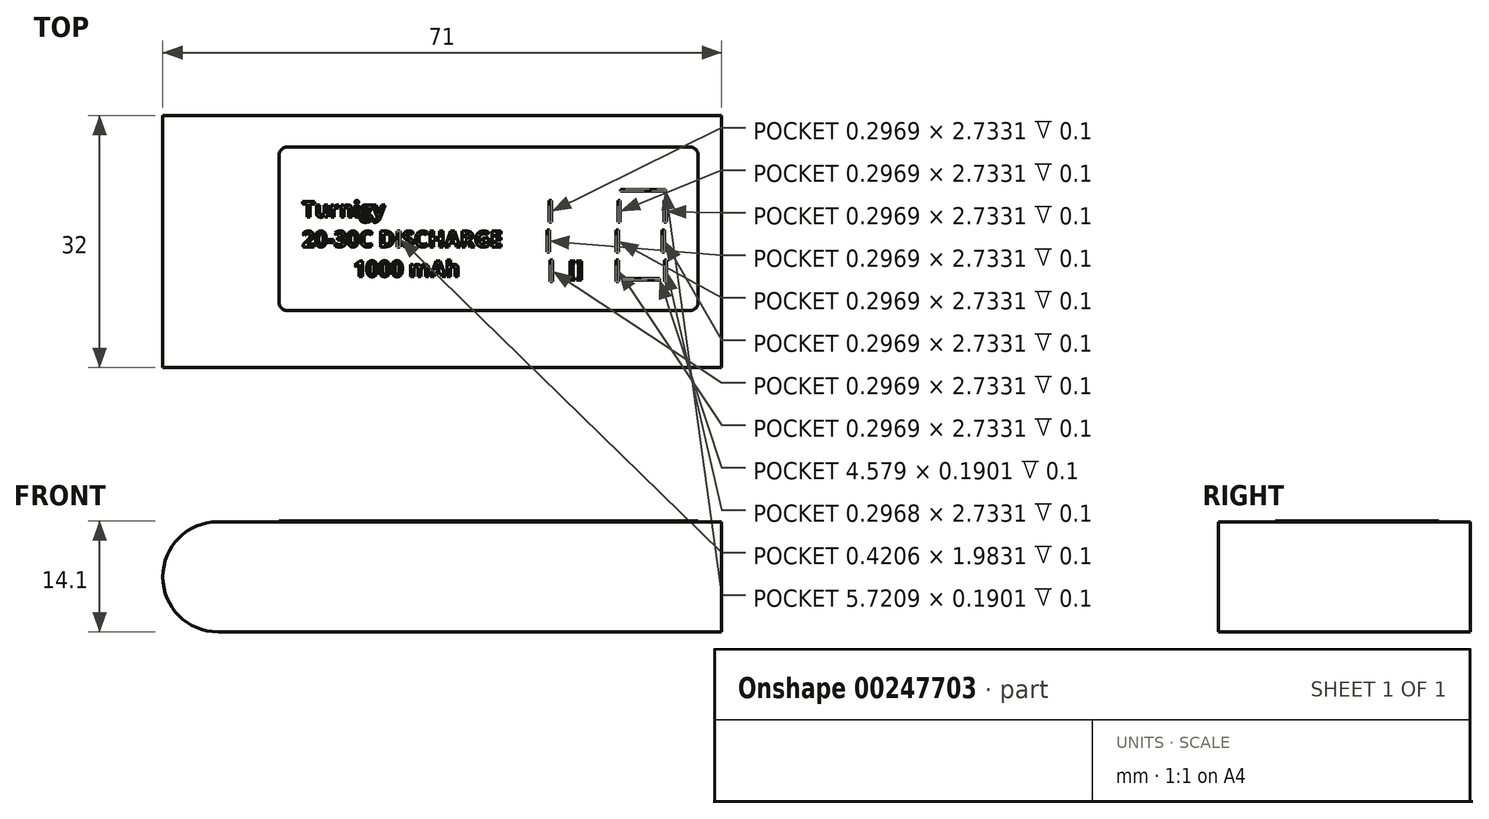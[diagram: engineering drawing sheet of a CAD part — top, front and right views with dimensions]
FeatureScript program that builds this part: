
annotation { "Feature Type Name" : "Feature", "Feature Type Description" : "" }
export const myFeature = defineFeature(function(context is Context, id is Id, definition is map)
    precondition{}
    {
        {
            var Q0;
            Q0=qCreatedBy(makeId("Top.planeOp"),FACE);
            var sketch = newSketch(context, id + "F0", { "sketchPlane" : qUnion([Q0])});
            skLineSegment(sketch, "E0.bottom", {"start": v(-40.56, 15.94) * mm, "end": v(30.44, 15.94) * mm});
            skLineSegment(sketch, "E0.top", {"start": v(-40.56, -16.06) * mm, "end": v(30.44, -16.06) * mm});
            skLineSegment(sketch, "E0.left", {"start": v(-40.56, 15.94) * mm, "end": v(-40.56, -16.06) * mm});
            skLineSegment(sketch, "E0.right", {"start": v(30.44, 15.94) * mm, "end": v(30.44, -16.06) * mm});
            skSolve(sketch);
        }
        {
            var Q0;
            Q0 = qSketchRegion(id + "F0", true);
            extrude(context, id + "F1", {"entities" : qUnion([Q0]), "depth" : 14 * mm});
        }
        {
            var Q0;
            Q0=makeQuery(id+"F1.opExtrude","CAP_EDGE",EDGE,{"disambiguationData":[OSD([sQuery(id+"F0.wireOp",EDGE,"E0.left")])],"isStart":false});
            var Q1;
            Q1=makeQuery(id+"F1.opExtrude","CAP_EDGE",EDGE,{"disambiguationData":[OSD([sQuery(id+"F0.wireOp",EDGE,"E0.left")])],"isStart":true});
            fillet(context, id + "F2", {"entities" : qUnion([Q0, Q1]), "radius" : 7 * mm, "tangentPropagation" : true, "allowEdgeOverflow" : false});
        }
        {
            var Q0;
            Q0=makeQuery(id+"F1.opExtrude","CAP_FACE",FACE,{"disambiguationData":[OSD([sQuery(id+"F0.wireOp",EDGE,"E0.bottom"),sQuery(id+"F0.wireOp",EDGE,"E0.top"),sQuery(id+"F0.wireOp",EDGE,"E0.left"),sQuery(id+"F0.wireOp",EDGE,"E0.right")])],"isStart":false});
            var sketch = newSketch(context, id + "F3", { "sketchPlane" : qUnion([Q0])});
            skText(sketch, "E1", { "text": "                                                        _____\nTurnigy                            |          |      |\n20-30C DISCHARGE       |          |      |\n         1000 mAh               |  []     |____|", "fontName": "OpenSans-Bold.ttf"});
            skLineSegment(sketch, "E2.bottom", {"start": v(-24.78, 11.94) * mm, "end": v(26.44, 11.94) * mm});
            skLineSegment(sketch, "E2.top", {"start": v(-24.78, -8.82) * mm, "end": v(26.44, -8.82) * mm});
            skLineSegment(sketch, "E2.left", {"start": v(-25.78, 10.94) * mm, "end": v(-25.78, -7.82) * mm});
            skLineSegment(sketch, "E2.right", {"start": v(27.44, 10.94) * mm, "end": v(27.44, -7.82) * mm});
            skPoint(sketch, "E3.visualSharp", {"position": v(-25.78, 11.94) * mm});
            skArc(sketch, "E3.filletArc", {"start": v(-24.78, 11.94) * mm, "mid": v(-25.49, 11.64) * mm, "end": v(-25.78, 10.94) * mm});
            skPoint(sketch, "E4.visualSharp", {"position": v(-25.78, -8.82) * mm});
            skArc(sketch, "E4.filletArc", {"start": v(-25.78, -7.82) * mm, "mid": v(-25.49, -8.52) * mm, "end": v(-24.78, -8.82) * mm});
            skPoint(sketch, "E5.visualSharp", {"position": v(27.44, 11.94) * mm});
            skArc(sketch, "E5.filletArc", {"start": v(27.44, 10.94) * mm, "mid": v(27.15, 11.64) * mm, "end": v(26.44, 11.94) * mm});
            skPoint(sketch, "E6.visualSharp", {"position": v(27.44, -8.82) * mm});
            skArc(sketch, "E6.filletArc", {"start": v(26.44, -8.82) * mm, "mid": v(27.15, -8.52) * mm, "end": v(27.44, -7.82) * mm});
            const initialGuessF3  = {"E1": [-0.02285, 0.00682, 1, 0, 0.002]};
            skSetInitialGuess(sketch, initialGuessF3);
            skSolve(sketch);
        }
        {
            var Q0;
            Q0=makeQuery(id+"F3.imprint","IMPRINT",FACE,{"disambiguationData":[TD([[makeQuery(id+"F3.imprint","IMPRINT",EDGE,{"derivedFrom":sQuery(id+"F3.wireOp",EDGE,"E1.sketch_text.stroke-122")}),1.0]])]});
            var Q1;
            Q1=makeQuery(id+"F3.imprint","IMPRINT",FACE,{"disambiguationData":[TD([[makeQuery(id+"F3.imprint","IMPRINT",EDGE,{"derivedFrom":sQuery(id+"F3.wireOp",EDGE,"E1.sketch_text.stroke-113")}),1.0]])]});
            var Q2;
            Q2=makeQuery(id+"F3.imprint","IMPRINT",FACE,{"disambiguationData":[TD([[makeQuery(id+"F3.imprint","IMPRINT",EDGE,{"derivedFrom":sQuery(id+"F3.wireOp",EDGE,"E1.sketch_text.stroke-189")}),1.0]])]});
            var Q3;
            Q3=makeQuery(id+"F3.imprint","IMPRINT",FACE,{"disambiguationData":[TD([[makeQuery(id+"F3.imprint","IMPRINT",EDGE,{"derivedFrom":sQuery(id+"F3.wireOp",EDGE,"E1.sketch_text.stroke-236")}),1.0]])]});
            var Q4;
            Q4=makeQuery(id+"F3.imprint","IMPRINT",FACE,{"disambiguationData":[TD([[makeQuery(id+"F3.imprint","IMPRINT",EDGE,{"derivedFrom":sQuery(id+"F3.wireOp",EDGE,"E1.sketch_text.stroke-266")}),1.0]])]});
            var Q5;
            Q5=makeQuery(id+"F3.imprint","IMPRINT",FACE,{"disambiguationData":[TD([[makeQuery(id+"F3.imprint","IMPRINT",EDGE,{"derivedFrom":sQuery(id+"F3.wireOp",EDGE,"E1.sketch_text.stroke-338")}),1.0]])]});
            var Q6;
            Q6=makeQuery(id+"F3.imprint","IMPRINT",FACE,{"disambiguationData":[TD([[makeQuery(id+"F3.imprint","IMPRINT",EDGE,{"derivedFrom":sQuery(id+"F3.wireOp",EDGE,"E1.sketch_text.stroke-342")}),1.0]])]});
            var Q7;
            Q7=makeQuery(id+"F3.imprint","IMPRINT",FACE,{"disambiguationData":[TD([[makeQuery(id+"F3.imprint","IMPRINT",EDGE,{"derivedFrom":sQuery(id+"F3.wireOp",EDGE,"E1.sketch_text.stroke-498")}),1.0]])]});
            var Q8;
            Q8=makeQuery(id+"F3.imprint","IMPRINT",FACE,{"disambiguationData":[TD([[makeQuery(id+"F3.imprint","IMPRINT",EDGE,{"derivedFrom":sQuery(id+"F3.wireOp",EDGE,"E1.sketch_text.stroke-454")}),1.0]])]});
            var Q9;
            Q9=makeQuery(id+"F3.imprint","IMPRINT",FACE,{"disambiguationData":[TD([[makeQuery(id+"F3.imprint","IMPRINT",EDGE,{"derivedFrom":sQuery(id+"F3.wireOp",EDGE,"E1.sketch_text.stroke-438")}),1.0]])]});
            var Q10;
            Q10=makeQuery(id+"F3.imprint","IMPRINT",FACE,{"disambiguationData":[TD([[makeQuery(id+"F3.imprint","IMPRINT",EDGE,{"derivedFrom":sQuery(id+"F3.wireOp",EDGE,"E1.sketch_text.stroke-422")}),1.0]])]});
            var Q11;
            {var subQ38=sQuery(id+"F3.wireOp",EDGE,"E1.sketch_text.stroke-0");Q11=makeQuery(id+"F3.imprint","IMPRINT",FACE,{"disambiguationData":[TD([[makeQuery(id+"F3.imprint","IMPRINT",EDGE,{"derivedFrom":subQ38}),1.0]])]});}
            extrude(context, id + "F4", {"entities" : qUnion([Q0, Q1, Q2, Q3, Q4, Q5, Q6, Q7, Q8, Q9, Q10, Q11]), "operationType" : NewBodyOperationType.ADD, "depth" : .1 * mm});
        }
    });
